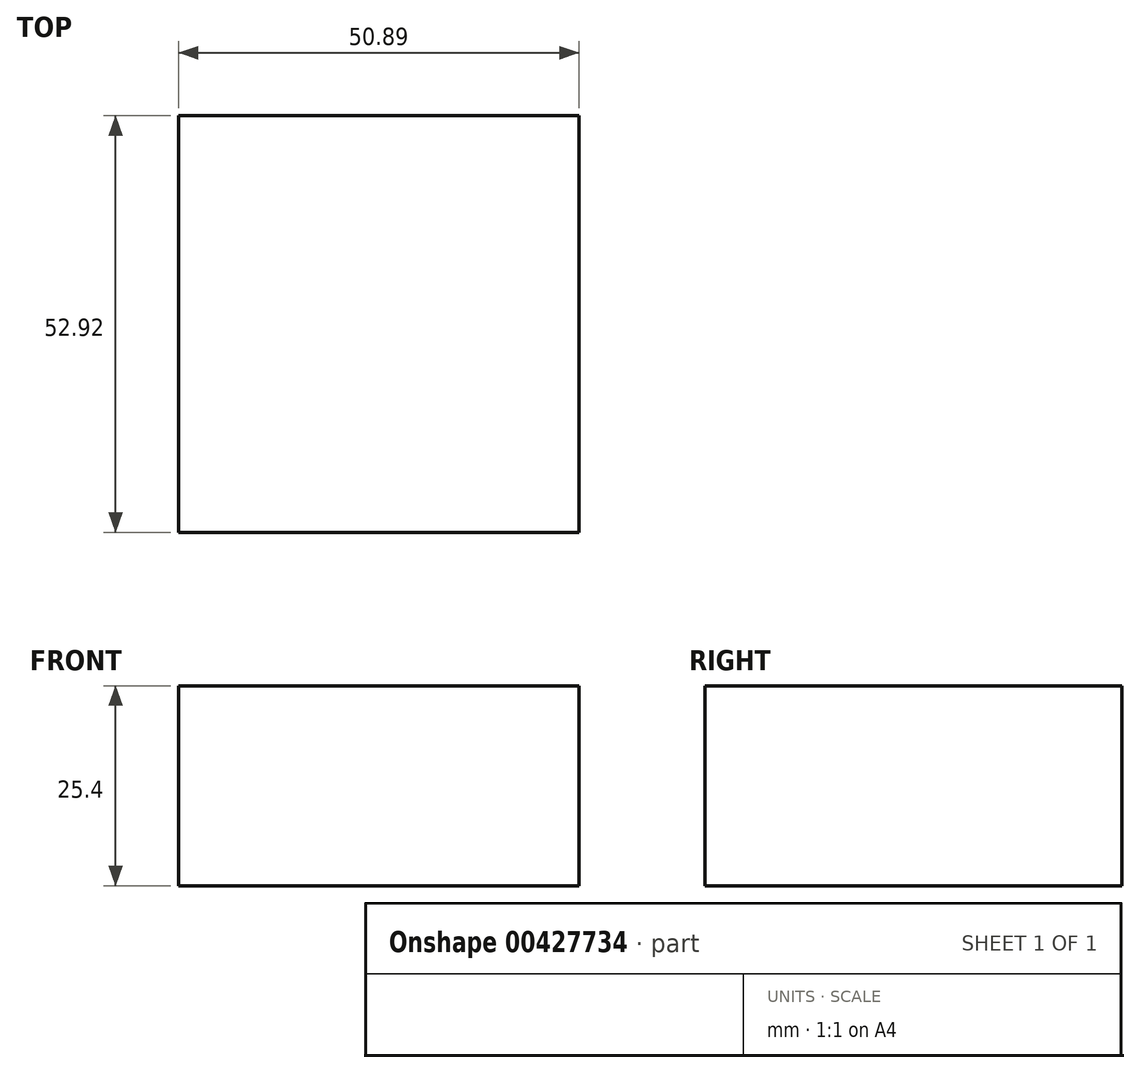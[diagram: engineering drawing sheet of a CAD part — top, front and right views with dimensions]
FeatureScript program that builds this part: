
annotation { "Feature Type Name" : "Feature", "Feature Type Description" : "" }
export const myFeature = defineFeature(function(context is Context, id is Id, definition is map)
    precondition{}
    {
        {
            var Q0;
            Q0=qCreatedBy(makeId("Top.planeOp"),FACE);
            var sketch = newSketch(context, id + "F0", { "sketchPlane" : qUnion([Q0])});
            skLineSegment(sketch, "E0.bottom", {"start": v(-25.41, 0) * mm, "end": v(25.48, 0) * mm});
            skLineSegment(sketch, "E0.top", {"start": v(-25.41, -52.92) * mm, "end": v(25.48, -52.92) * mm});
            skLineSegment(sketch, "E0.left", {"start": v(-25.41, 0) * mm, "end": v(-25.41, -52.92) * mm});
            skLineSegment(sketch, "E0.right", {"start": v(25.48, 0) * mm, "end": v(25.48, -52.92) * mm});
            skSolve(sketch);
        }
        {
            var Q0;
            Q0=makeQuery(id+"F0.imprint","IMPRINT",FACE,{"disambiguationData":[TD([[makeQuery(id+"F0.imprint","IMPRINT",EDGE,{"derivedFrom":sQuery(id+"F0.wireOp",EDGE,"E0.bottom")}),-1.0]])]});
            var Q1;
            Q1=sQuery(id+"F0.wireOp",EDGE,"E0.left");
            var Q2;
            Q2=sQuery(id+"F0.wireOp",EDGE,"E0.top");
            var Q3;
            Q3=sQuery(id+"F0.wireOp",EDGE,"E0.right");
            var Q4;
            Q4=sQuery(id+"F0.wireOp",EDGE,"E0.bottom");
            extrude(context, id + "F1", {"entities" : qUnion([Q0]), "bodyType" : ToolBodyType.SURFACE, "surfaceEntities" : qUnion([Q1, Q2, Q3, Q4]), "oppositeDirection" : true, "depth" : 25.4 * mm});
        }
    });
